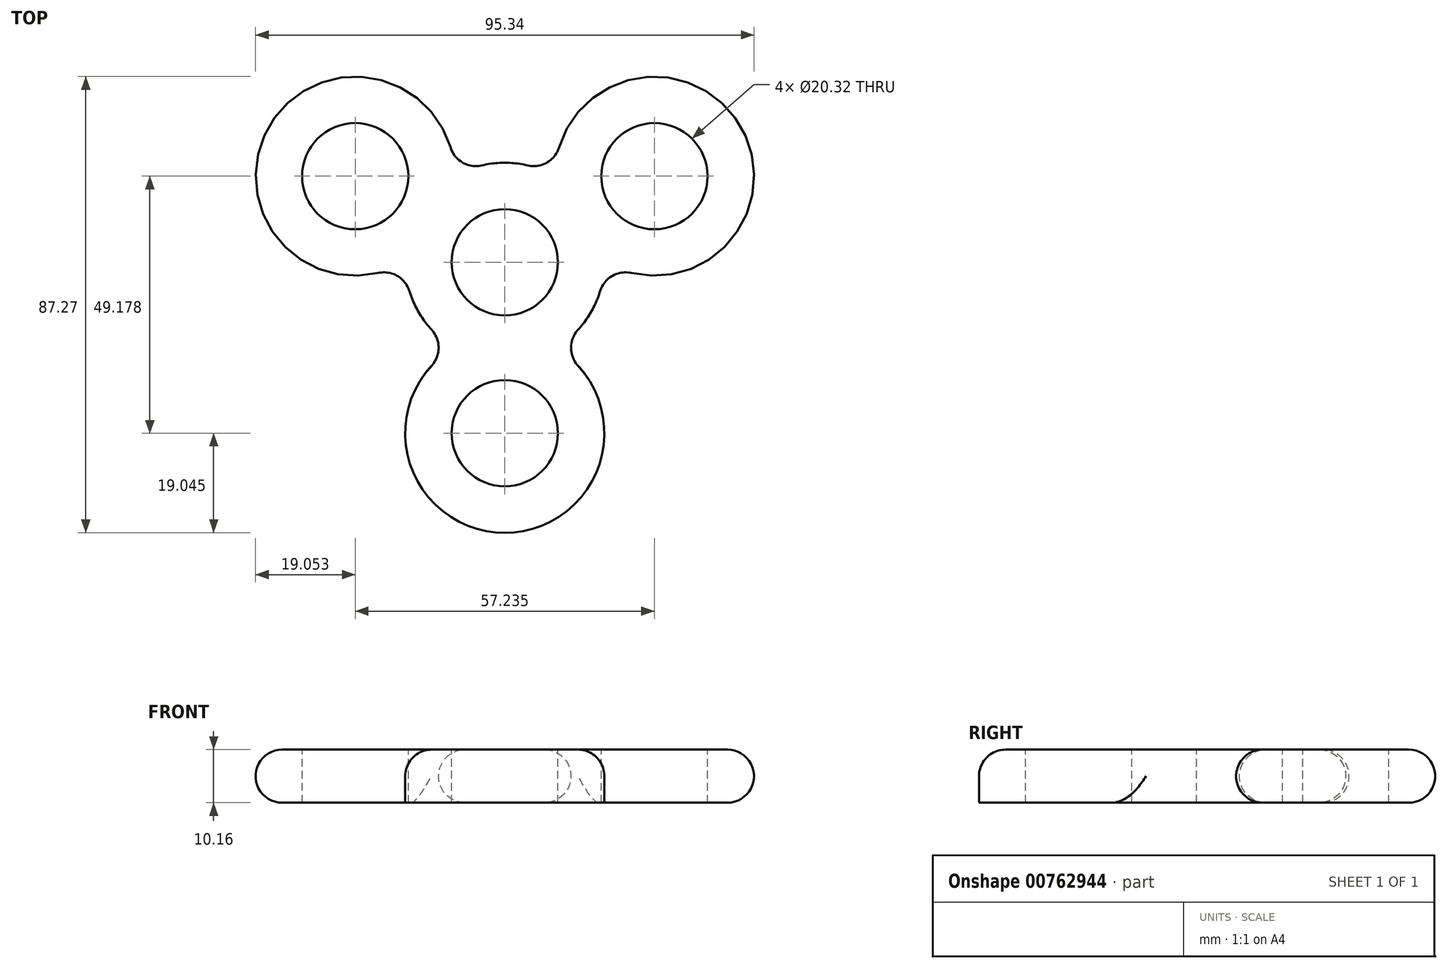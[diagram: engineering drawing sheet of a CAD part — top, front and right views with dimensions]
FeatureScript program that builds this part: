
annotation { "Feature Type Name" : "Feature", "Feature Type Description" : "" }
export const myFeature = defineFeature(function(context is Context, id is Id, definition is map)
    precondition{}
    {
        {
            var Q0;
            Q0=qCreatedBy(makeId("Top.planeOp"),FACE);
            var sketch = newSketch(context, id + "F0", { "sketchPlane" : qUnion([Q0])});
            skCircle(sketch, "E0", {"center": v(0, 0) * mm, "radius": 19.05 * mm});
            skPoint(sketch, "E1", {"position": v(-19.05, 0) * mm});
            skPoint(sketch, "E2", {"position": v(19.05, 0) * mm});
            skArc(sketch, "E3", {"start": v(19.05, 0) * mm, "mid": v(45.13, 25.98) * mm, "end": v(9.57, 16.47) * mm});
            skPoint(sketch, "E3.second.point", {"position": v(42.86, 3.82) * mm});
            skPoint(sketch, "E3.third.point", {"position": v(38.18, 0) * mm});
            skArc(sketch, "E4", {"start": v(-9.57, 16.47) * mm, "mid": v(-45.13, 25.98) * mm, "end": v(-19.05, 0) * mm});
            skPoint(sketch, "E4.second.point", {"position": v(-42.86, 3.82) * mm});
            skPoint(sketch, "E4.third.point", {"position": v(-38.18, 0) * mm});
            skArc(sketch, "E5.MirrorC", {"start": v(9.77, -16.35) * mm, "mid": v(0, -51.75) * mm, "end": v(-9.77, -16.35) * mm});
            skSolve(sketch);
        }
        {
            var Q0;
            Q0 = qSketchRegion(id + "F0", true);
            extrude(context, id + "F1", {"entities" : qUnion([Q0]), "depth" : 10.16 * mm, "offsetDistance" : 25.4 * mm});
        }
        {
            var Q0;
            Q0=makeQuery(id+"F1.opExtrude","SWEPT_FACE",FACE,{"disambiguationData":[OSD([sQuery(id+"F0.wireOp",EDGE,"E4")])]});
            var Q1;
            Q1=makeQuery(id+"F1.opExtrude","CAP_EDGE",EDGE,{"disambiguationData":[OSD([sQuery(id+"F0.wireOp",EDGE,"E5.MirrorC")])],"isStart":false});
            var Q2;
            {var subQ0=sQuery(id+"F0.wireOp",EDGE,"E0");Q2=makeQuery(id+"F1.opExtrude","CAP_EDGE",EDGE,{"disambiguationData":[OSD([subQ0]),TDD([makeQuery(id+"F0.imprint","IMPRINT",EDGE,{"disambiguationData":[TD([[makeQuery(id+"F0.imprint","INTERSECT",VERTEX,{"disambiguationData":[OD(0.0)],"derivedFrom":[subQ0,sQuery(id+"F0.wireOp",EDGE,"E3")]}),1.0]])],"derivedFrom":subQ0})])],"isStart":false});}
            var Q3;
            {var subQ0=sQuery(id+"F0.wireOp",EDGE,"E0");Q3=makeQuery(id+"F1.opExtrude","SWEPT_FACE",FACE,{"disambiguationData":[OSD([subQ0]),TDD([makeQuery(id+"F0.imprint","IMPRINT",EDGE,{"disambiguationData":[TD([[makeQuery(id+"F0.imprint","INTERSECT",VERTEX,{"disambiguationData":[OD(1.0)],"derivedFrom":[subQ0,sQuery(id+"F0.wireOp",EDGE,"E4")]}),-1.0]])],"derivedFrom":subQ0})])]});}
            var Q4;
            Q4=makeQuery(id+"F1.opExtrude","SWEPT_FACE",FACE,{"disambiguationData":[OSD([sQuery(id+"F0.wireOp",EDGE,"E3")])]});
            var Q5;
            {var subQ0=sQuery(id+"F0.wireOp",EDGE,"E0");Q5=makeQuery(id+"F1.opExtrude","SWEPT_FACE",FACE,{"disambiguationData":[OSD([subQ0]),TDD([makeQuery(id+"F0.imprint","IMPRINT",EDGE,{"disambiguationData":[TD([[makeQuery(id+"F0.imprint","INTERSECT",VERTEX,{"disambiguationData":[OD(1.0)],"derivedFrom":[subQ0,sQuery(id+"F0.wireOp",EDGE,"E3")]}),-1.0]])],"derivedFrom":subQ0})])]});}
            var Q6;
            {var subQ0=sQuery(id+"F0.wireOp",EDGE,"E0");Q6=makeQuery(id+"F1.opExtrude","SWEPT_FACE",FACE,{"disambiguationData":[OSD([subQ0]),TDD([makeQuery(id+"F0.imprint","IMPRINT",EDGE,{"disambiguationData":[TD([[makeQuery(id+"F0.imprint","INTERSECT",VERTEX,{"disambiguationData":[OD(0.0)],"derivedFrom":[subQ0,sQuery(id+"F0.wireOp",EDGE,"E3")]}),1.0]])],"derivedFrom":subQ0})])]});}
            fillet(context, id + "F2", {"entities" : qUnion([Q0, Q1, Q2, Q3, Q4, Q5, Q6]), "radius" : 5.08 * mm, "tangentPropagation" : true, "allowEdgeOverflow" : false});
        }
        {
            var Q0;
            Q0=makeQuery(id+"F1.opExtrude","CAP_FACE",FACE,{"disambiguationData":[OSD([sQuery(id+"F0.wireOp",EDGE,"E0"),sQuery(id+"F0.wireOp",EDGE,"E3"),sQuery(id+"F0.wireOp",EDGE,"E4"),sQuery(id+"F0.wireOp",EDGE,"E5.MirrorC")])],"isStart":false});
            var sketch = newSketch(context, id + "F3", { "sketchPlane" : qUnion([Q0])});
            skCircle(sketch, "E6", {"center": v(0, 0) * mm, "radius": 10.16 * mm});
            skCircle(sketch, "E7", {"center": v(0, -32.7) * mm, "radius": 10.16 * mm});
            skCircle(sketch, "E8", {"center": v(28.62, 16.47) * mm, "radius": 10.16 * mm});
            skCircle(sketch, "E9", {"center": v(-28.62, 16.47) * mm, "radius": 10.16 * mm});
            skSolve(sketch);
        }
        {
            var Q0;
            Q0=sQuery(id+"F3.wireOp",VERTEX,"E6.center");
            var Q1;
            Q1=sQuery(id+"F3.wireOp",VERTEX,"E9.center");
            var Q2;
            Q2=sQuery(id+"F3.wireOp",VERTEX,"E7.center");
            var Q3;
            Q3=sQuery(id+"F3.wireOp",VERTEX,"E8.center");
            var Q4;
            Q4=makeQuery(id+"F1.opExtrude","SWEPT_BODY",BODY,{"disambiguationData":[OSD([sQuery(id+"F0.wireOp",EDGE,"E0"),sQuery(id+"F0.wireOp",EDGE,"E3"),sQuery(id+"F0.wireOp",EDGE,"E4"),sQuery(id+"F0.wireOp",EDGE,"E5.MirrorC")])]});
            hole(context, id + "F4", {"style" : HoleStyle.SIMPLE, "endStyle" : HoleEndStyle.THROUGH, "holeDiameter" : 20.32 * mm, "majorDiameter" : 6.35 * mm, "isTappedThrough" : true, "tappedDepth" : 12.7 * mm, "tapClearance" : 3, "locations" : qUnion([Q0, Q1, Q2, Q3]), "scope" : qUnion([Q4])});
        }
    });
